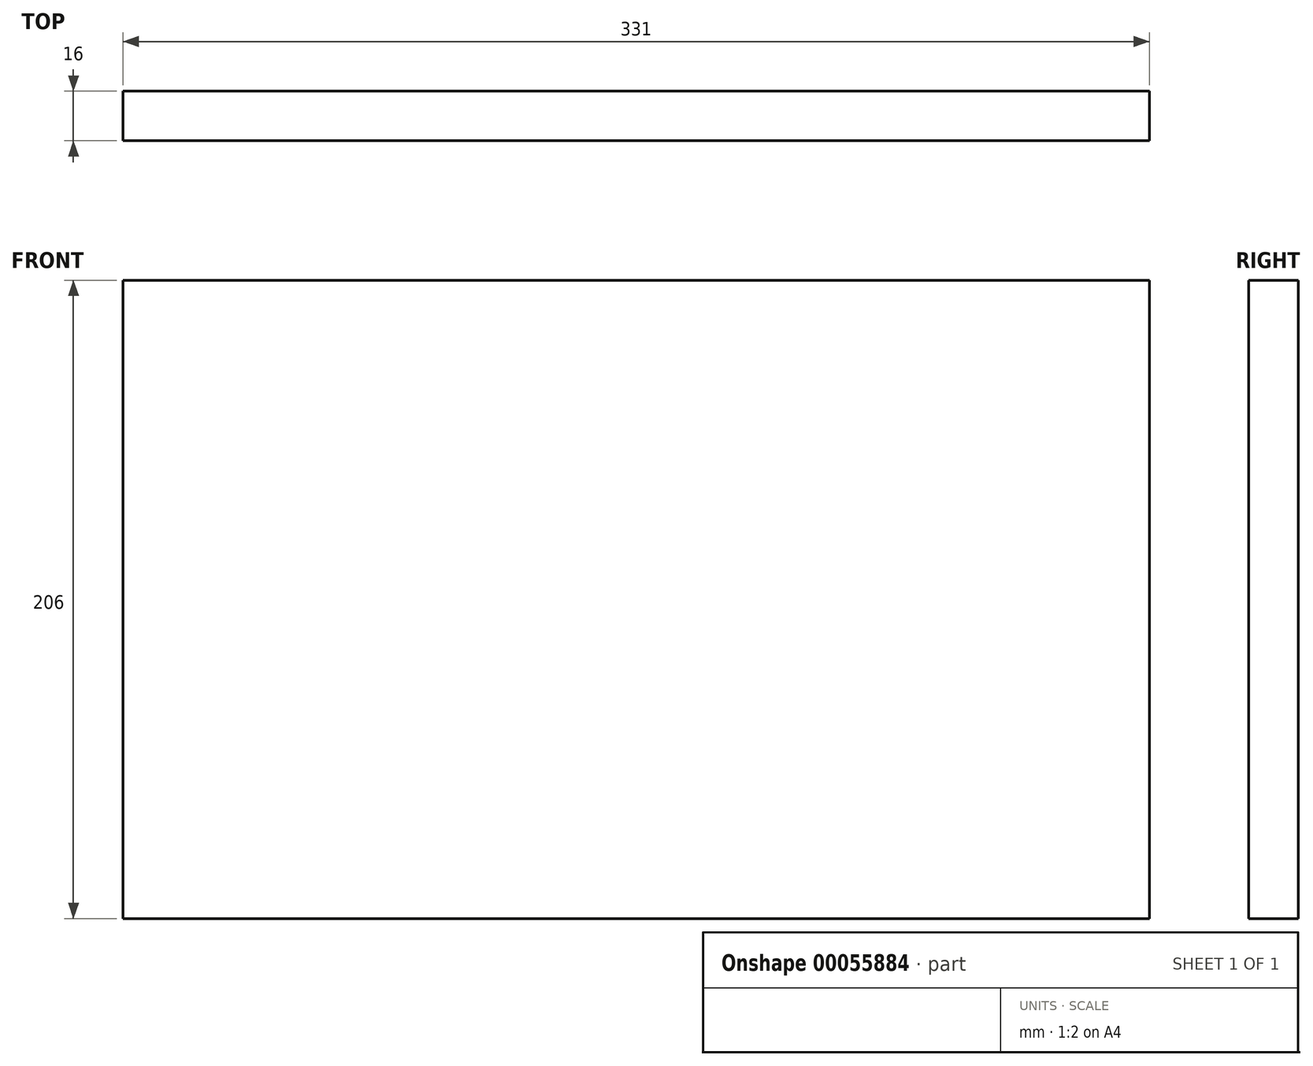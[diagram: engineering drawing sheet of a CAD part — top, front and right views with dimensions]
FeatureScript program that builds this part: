
annotation { "Feature Type Name" : "Feature", "Feature Type Description" : "" }
export const myFeature = defineFeature(function(context is Context, id is Id, definition is map)
    precondition{}
    {
        {
            var Q0;
            Q0=qCreatedBy(makeId("Front.planeOp"),FACE);
            var sketch = newSketch(context, id + "F0", { "sketchPlane" : qUnion([Q0])});
            skLineSegment(sketch, "E0.rect.bottom", {"start": v(-165.5, 103) * mm, "end": v(165.5, 103) * mm});
            skLineSegment(sketch, "E0.rect.top", {"start": v(-165.5, -103) * mm, "end": v(165.5, -103) * mm});
            skLineSegment(sketch, "E0.rect.left", {"start": v(-165.5, 103) * mm, "end": v(-165.5, -103) * mm});
            skLineSegment(sketch, "E0.rect.right", {"start": v(165.5, 103) * mm, "end": v(165.5, -103) * mm});
            skPoint(sketch, "E0.rect.middle", {"position": v(0, 0) * mm});
            skSolve(sketch);
        }
        {
            var Q0;
            Q0=makeQuery(id+"F0.imprint","IMPRINT",FACE,{"disambiguationData":[TD([[makeQuery(id+"F0.imprint","IMPRINT",EDGE,{"derivedFrom":sQuery(id+"F0.wireOp",EDGE,"E0.rect.bottom")}),-1.0]])]});
            extrude(context, id + "F1", {"entities" : qUnion([Q0]), "oppositeDirection" : true, "depth" : 16 * mm});
        }
    });
